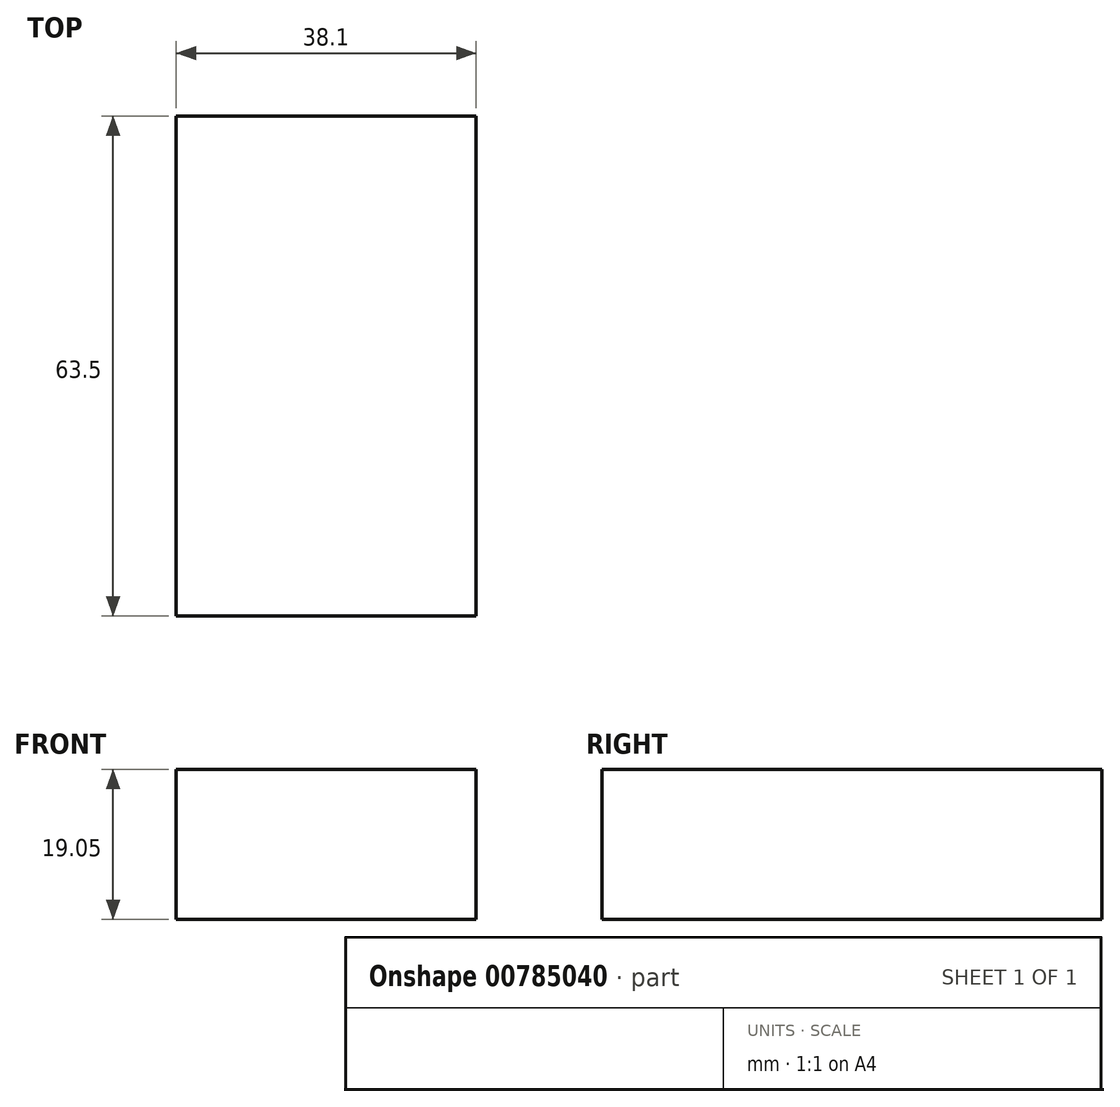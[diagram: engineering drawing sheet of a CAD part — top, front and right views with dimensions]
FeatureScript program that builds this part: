
annotation { "Feature Type Name" : "Feature", "Feature Type Description" : "" }
export const myFeature = defineFeature(function(context is Context, id is Id, definition is map)
    precondition{}
    {
        {
            var Q0;
            Q0=qCreatedBy(makeId("Top.planeOp"),FACE);
            var sketch = newSketch(context, id + "F0", { "sketchPlane" : qUnion([Q0])});
            skLineSegment(sketch, "E0.bottom", {"start": v(0, 0) * mm, "end": v(38.1, 0) * mm});
            skLineSegment(sketch, "E0.top", {"start": v(0, 63.5) * mm, "end": v(38.1, 63.5) * mm});
            skLineSegment(sketch, "E0.left", {"start": v(0, 0) * mm, "end": v(0, 63.5) * mm});
            skLineSegment(sketch, "E0.right", {"start": v(38.1, 0) * mm, "end": v(38.1, 63.5) * mm});
            skSolve(sketch);
        }
        {
            var Q0;
            Q0 = qSketchRegion(id + "F0", true);
            extrude(context, id + "F1", {"entities" : qUnion([Q0]), "depth" : 19.05 * mm, "offsetDistance" : 25.4 * mm});
        }
    });
